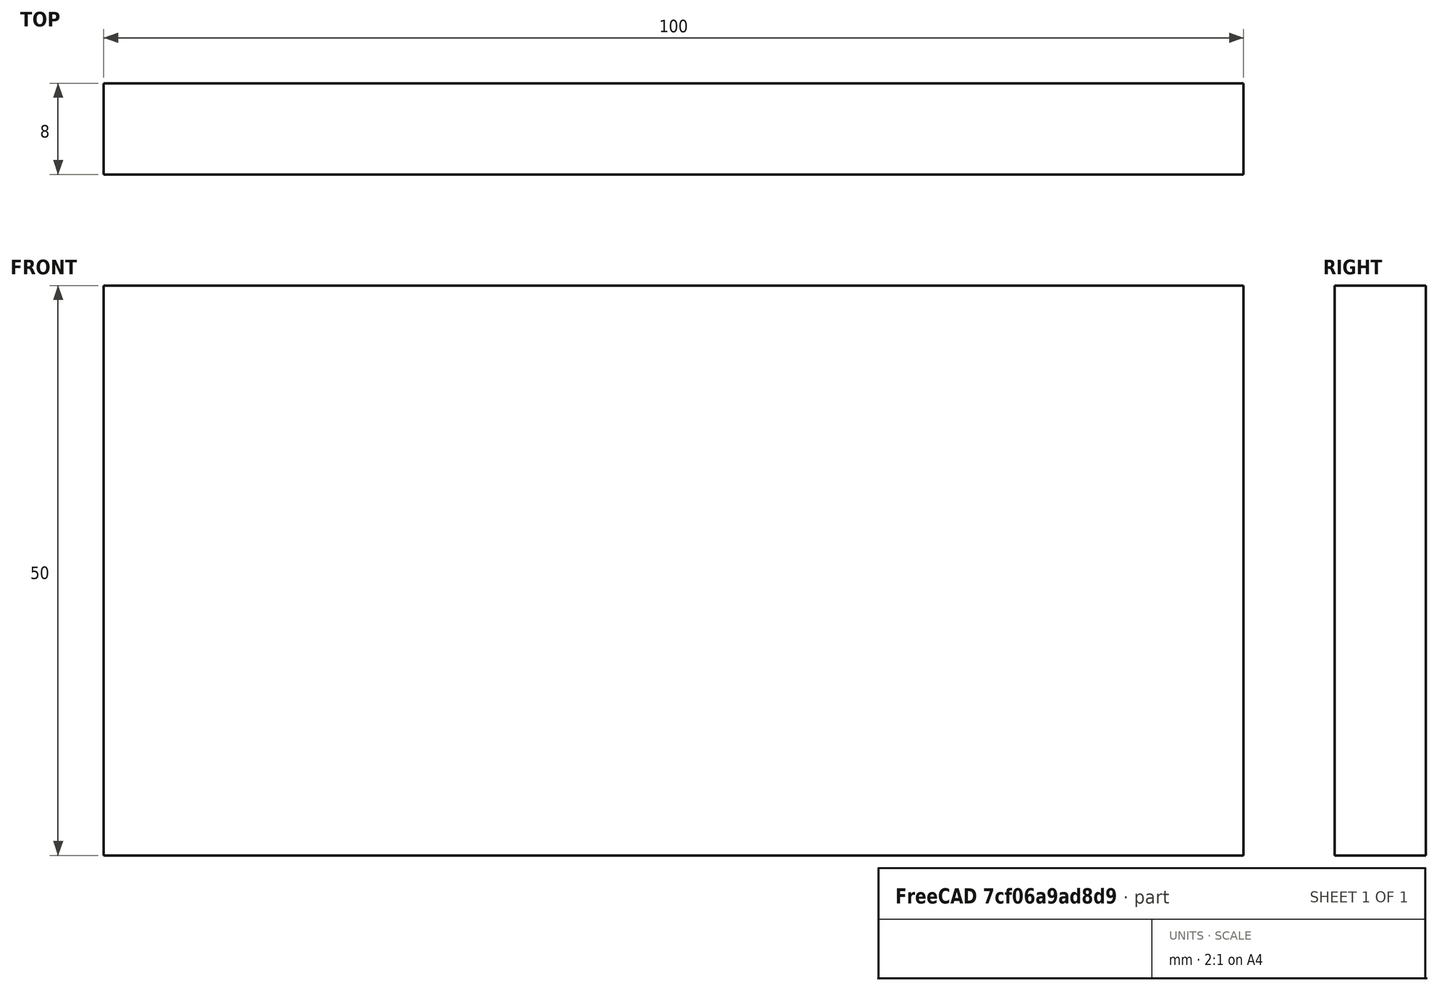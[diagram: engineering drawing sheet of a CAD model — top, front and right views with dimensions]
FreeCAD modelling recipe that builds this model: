
FCSTD DOCUMENT  (FreeCAD 0.15R4671 (Git))
Label: Flat Bar 100x8 EN10058 S235JR
License: All rights reserved
LicenseURL: http://en.wikipedia.org/wiki/All_rights_reserved
objects: Sketcher::SketchObject×1, Part::Extrusion×1
note: 2 computed .brp shape members not serialized (recipe doc carries the construction recipe); baked Part::Feature solids carry a one-line shape summary decoded from their .brp

FEATURE [Sketcher::SketchObject] Sketch
  sketch-geometry (4):
    g0: LineSegment StartX=-50 StartY=-4 StartZ=0 EndX=50 EndY=-4 EndZ=0
    g1: LineSegment StartX=50 StartY=-4 StartZ=0 EndX=50 EndY=4 EndZ=0
    g2: LineSegment StartX=50 StartY=4 StartZ=0 EndX=-50 EndY=4 EndZ=0
    g3: LineSegment StartX=-50 StartY=4 StartZ=0 EndX=-50 EndY=-4 EndZ=0
  constraints (12):
    c: Coincident(g0,g1)
    c: Coincident(g1,g2)
    c: Coincident(g2,g3)
    c: Coincident(g3,g0)
    c: Horizontal(g0)
    c: Horizontal(g2)
    c: Vertical(g1)
    c: Vertical(g3)
    c: Symmetric(g1,g2,g-2)
    c: Symmetric(g0,g1,g-1)
    c: DistanceY(g1) = 8
    c: DistanceX(g0) = 100
FEATURE [Part::Extrusion] Extrude  label="Flat Bar 100x8 EN10058 S235JR"
  Base = -> Sketch
  Dir = (0,0,50)
  Solid = true
